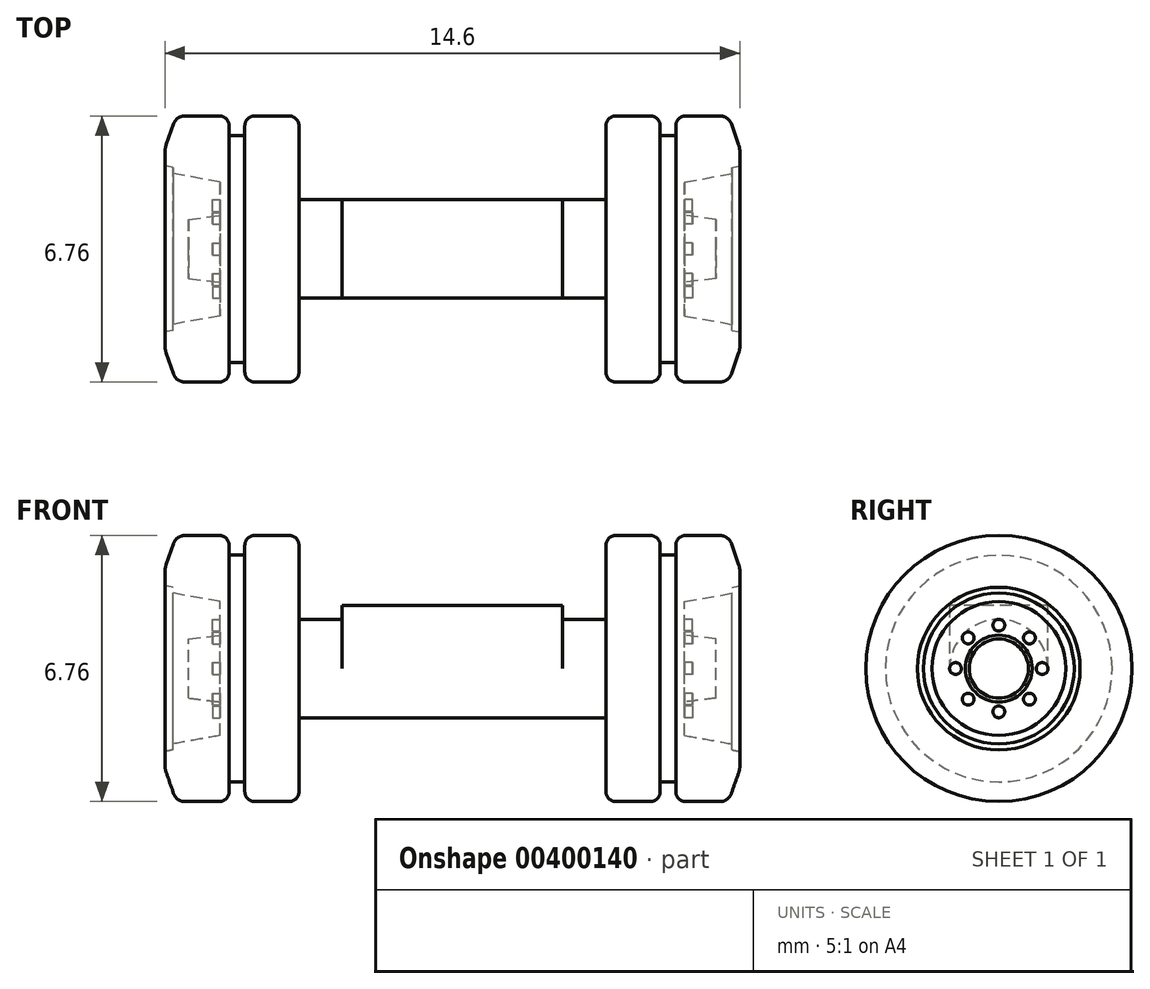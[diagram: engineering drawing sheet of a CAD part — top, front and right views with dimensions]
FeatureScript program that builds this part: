
annotation { "Feature Type Name" : "Feature", "Feature Type Description" : "" }
export const myFeature = defineFeature(function(context is Context, id is Id, definition is map)
    precondition{}
    {
        {
            var Q0;
            Q0=qCreatedBy(makeId("Front.planeOp"),FACE);
            var sketch = newSketch(context, id + "F0", { "sketchPlane" : qUnion([Q0])});
            skLineSegment(sketch, "E0", {"start": v(0, 0) * mm, "end": v(-36.36, 0) * mm, "construction": true});
            skLineSegment(sketch, "E1", {"start": v(0, 0) * mm, "end": v(0, 0.75) * mm});
            skLineSegment(sketch, "E2", {"start": v(-0.8, 0.85) * mm, "end": v(-0.8, 1.7) * mm});
            skLineSegment(sketch, "E3", {"start": v(-0.8, 1.7) * mm, "end": v(0.4, 1.92) * mm});
            skLineSegment(sketch, "E4", {"start": v(0.6, 2.15) * mm, "end": v(0.6, 2.48) * mm});
            skLineSegment(sketch, "E5", {"start": v(0.1, 3.38) * mm, "end": v(-0.78, 3.38) * mm});
            skLineSegment(sketch, "E6", {"start": v(-1.03, 3.13) * mm, "end": v(-1.03, 2.88) * mm});
            skLineSegment(sketch, "E7", {"start": v(-1.03, 2.88) * mm, "end": v(-1.43, 2.88) * mm});
            skLineSegment(sketch, "E8", {"start": v(-1.43, 2.88) * mm, "end": v(-1.43, 3.13) * mm});
            skLineSegment(sketch, "E9", {"start": v(-1.67, 3.38) * mm, "end": v(-2.55, 3.38) * mm});
            skLineSegment(sketch, "E10", {"start": v(-2.8, 3.13) * mm, "end": v(-2.8, 1.25) * mm});
            skLineSegment(sketch, "E11", {"start": v(-3.9, 1.25) * mm, "end": v(-3.9, 0) * mm});
            skLineSegment(sketch, "E12", {"start": v(-3.9, 0) * mm, "end": v(0, 0) * mm});
            skLineSegment(sketch, "E13", {"start": v(0.4, 1.92) * mm, "end": v(0.4, 2.07) * mm});
            skLineSegment(sketch, "E14", {"start": v(0.4, 2.07) * mm, "end": v(0.56, 2.1) * mm});
            skLineSegment(sketch, "E15", {"start": v(-3.9, 1.25) * mm, "end": v(-2.8, 1.25) * mm});
            skPoint(sketch, "E16.visualSharp", {"position": v(0.6, 3.38) * mm});
            skPoint(sketch, "E17.visualSharp", {"position": v(-2.8, 3.38) * mm});
            skArc(sketch, "E17.filletArc", {"start": v(-2.55, 3.38) * mm, "mid": v(-2.73, 3.3) * mm, "end": v(-2.8, 3.13) * mm});
            skPoint(sketch, "E18.visualSharp", {"position": v(-1.03, 3.38) * mm});
            skArc(sketch, "E18.filletArc", {"start": v(-0.78, 3.38) * mm, "mid": v(-0.95, 3.3) * mm, "end": v(-1.03, 3.13) * mm});
            skPoint(sketch, "E19.visualSharp", {"position": v(-1.43, 3.38) * mm});
            skArc(sketch, "E19.filletArc", {"start": v(-1.42, 3.13) * mm, "mid": v(-1.5, 3.3) * mm, "end": v(-1.67, 3.38) * mm});
            skPoint(sketch, "E20.visualSharp", {"position": v(0.6, 2.1) * mm});
            skArc(sketch, "E20.filletArc", {"start": v(0.56, 2.1) * mm, "mid": v(0.59, 2.12) * mm, "end": v(0.6, 2.15) * mm});
            skLineSegment(sketch, "E21", {"start": v(0.38, 3.18) * mm, "end": v(0.57, 2.65) * mm});
            skPoint(sketch, "E22.visualSharp", {"position": v(0.6, 2.57) * mm});
            skArc(sketch, "E22.filletArc", {"start": v(0.6, 2.48) * mm, "mid": v(0.6, 2.56) * mm, "end": v(0.57, 2.65) * mm});
            skPoint(sketch, "E23.visualSharp", {"position": v(0.31, 3.38) * mm});
            skArc(sketch, "E23.filletArc", {"start": v(0.38, 3.18) * mm, "mid": v(0.27, 3.32) * mm, "end": v(0.1, 3.38) * mm});
            skLineSegment(sketch, "E24", {"start": v(-0.8, 0.85) * mm, "end": v(0, 0.75) * mm});
            skSolve(sketch);
        }
        {
            var Q0;
            Q0=qSketchRegion(id+"F0",true);
            var Q1;
            Q1=sQuery(id+"F0.wireOp",EDGE,"E0");
            revolve(context, id + "F1", {"entities" : qUnion([Q0]), "axis" : qUnion([Q1]), "revolveType" : RevolveType.FULL});
        }
        {
            var Q0;
            Q0=makeQuery(id+"F1.opRevolve","SWEPT_FACE",FACE,{"disambiguationData":[OSD([sQuery(id+"F0.wireOp",EDGE,"E2")])]});
            var sketch = newSketch(context, id + "F2", { "sketchPlane" : qUnion([Q0])});
            skCircle(sketch, "E25", {"center": v(0, 0) * mm, "radius": 1.1 * mm, "construction": true});
            skCircle(sketch, "E26", {"center": v(0, 1.1) * mm, "radius": 0.15 * mm});
            skSolve(sketch);
        }
        {
            var Q0;
            Q0=qSketchRegion(id+"F2",true);
            extrude(context, id + "F3", {"entities" : qUnion([Q0]), "operationType" : NewBodyOperationType.ADD, "depth" : 0.2 * mm});
        }
        {
            var Q0;
            Q0=makeQuery(id+"F1.opRevolve","SWEPT_BODY",BODY,{"disambiguationData":[OSD([sQuery(id+"F0.wireOp",EDGE,"E1"),sQuery(id+"F0.wireOp",EDGE,"9i6tZyW2-yzXX-9EZJ-h79J-1cwnScpkviuc"),sQuery(id+"F0.wireOp",EDGE,"HbyUoBcI-ubs4-mTwl-hbnX-KPwjTuaUvTQE"),sQuery(id+"F0.wireOp",EDGE,"AccDx7tV-JdvI-fhYc-sTzn-GkBhagOZLKRE"),sQuery(id+"F0.wireOp",EDGE,"E2"),sQuery(id+"F0.wireOp",EDGE,"E3"),sQuery(id+"F0.wireOp",EDGE,"E4"),sQuery(id+"F0.wireOp",EDGE,"E5"),sQuery(id+"F0.wireOp",EDGE,"E6"),sQuery(id+"F0.wireOp",EDGE,"E7"),sQuery(id+"F0.wireOp",EDGE,"E8"),sQuery(id+"F0.wireOp",EDGE,"E9"),sQuery(id+"F0.wireOp",EDGE,"E10"),sQuery(id+"F0.wireOp",EDGE,"E11"),sQuery(id+"F0.wireOp",EDGE,"MRLpm4EO-d1Rz-y1Wd-tjo4-32WrfEVe7Kie"),sQuery(id+"F0.wireOp",EDGE,"1fY617z1-xQKE-QZae-sQAy-9TSEcJzTBgR6"),sQuery(id+"F0.wireOp",EDGE,"E12"),sQuery(id+"F0.wireOp",EDGE,"E13"),sQuery(id+"F0.wireOp",EDGE,"E14"),sQuery(id+"F0.wireOp",EDGE,"E15")])]});
            var Q1;
            Q1=makeQuery(id+"F1.opRevolve","SWEPT_FACE",FACE,{"disambiguationData":[OSD([sQuery(id+"F0.wireOp",EDGE,"E5")])]});
            circularPattern(context, id + "F4", {"operationType" : NewBodyOperationType.ADD, "entities" : qUnion([Q0]), "axis" : qUnion([Q1]), "angle" : 360 * degree, "instanceCount" : 8, "equalSpace" : true});
        }
        {
            var Q0;
            Q0=makeQuery(id+"F1.opRevolve","SWEPT_FACE",FACE,{"disambiguationData":[OSD([sQuery(id+"F0.wireOp",EDGE,"E11")])]});
            var sketch = newSketch(context, id + "F5", { "sketchPlane" : qUnion([Q0])});
            skArc(sketch, "E27.0", {"start": v(-1.25, 0) * mm, "mid": v(0, -1.25) * mm, "end": v(1.25, 0) * mm});
            skLineSegment(sketch, "E28", {"start": v(-1.25, 0) * mm, "end": v(-1.25, 1.6) * mm});
            skLineSegment(sketch, "E29", {"start": v(-1.25, 1.6) * mm, "end": v(1.25, 1.6) * mm});
            skLineSegment(sketch, "E30", {"start": v(1.25, 1.6) * mm, "end": v(1.25, 0) * mm});
            skSolve(sketch);
        }
        {
            var Q0;
            Q0=qSketchRegion(id+"F5",true);
            extrude(context, id + "F6", {"entities" : qUnion([Q0]), "operationType" : NewBodyOperationType.ADD, "depth" : 2.8 * mm});
        }
        {
            var Q0;
            Q0=makeQuery(id+"F1.opRevolve","SWEPT_BODY",BODY,{"disambiguationData":[OSD([sQuery(id+"F0.wireOp",EDGE,"E1"),sQuery(id+"F0.wireOp",EDGE,"9i6tZyW2-yzXX-9EZJ-h79J-1cwnScpkviuc"),sQuery(id+"F0.wireOp",EDGE,"HbyUoBcI-ubs4-mTwl-hbnX-KPwjTuaUvTQE"),sQuery(id+"F0.wireOp",EDGE,"AccDx7tV-JdvI-fhYc-sTzn-GkBhagOZLKRE"),sQuery(id+"F0.wireOp",EDGE,"E2"),sQuery(id+"F0.wireOp",EDGE,"E3"),sQuery(id+"F0.wireOp",EDGE,"E4"),sQuery(id+"F0.wireOp",EDGE,"E5"),sQuery(id+"F0.wireOp",EDGE,"E6"),sQuery(id+"F0.wireOp",EDGE,"E7"),sQuery(id+"F0.wireOp",EDGE,"E8"),sQuery(id+"F0.wireOp",EDGE,"E9"),sQuery(id+"F0.wireOp",EDGE,"E10"),sQuery(id+"F0.wireOp",EDGE,"E11"),sQuery(id+"F0.wireOp",EDGE,"E12"),sQuery(id+"F0.wireOp",EDGE,"E13"),sQuery(id+"F0.wireOp",EDGE,"E14"),sQuery(id+"F0.wireOp",EDGE,"E15"),sQuery(id+"F0.wireOp",EDGE,"E16.filletArc"),sQuery(id+"F0.wireOp",EDGE,"E17.filletArc"),sQuery(id+"F0.wireOp",EDGE,"E18.filletArc"),sQuery(id+"F0.wireOp",EDGE,"E19.filletArc"),sQuery(id+"F0.wireOp",EDGE,"E20.filletArc")])]});
            var Q1;
            Q1=makeQuery(id+"F6.opExtrude","CAP_FACE",FACE,{"disambiguationData":[OSD([sQuery(id+"F5.wireOp",EDGE,"E27.0"),sQuery(id+"F5.wireOp",EDGE,"E28"),sQuery(id+"F5.wireOp",EDGE,"E29"),sQuery(id+"F5.wireOp",EDGE,"E30")])],"isStart":false});
            mirror(context, id + "F7", {"operationType" : NewBodyOperationType.ADD, "entities" : qUnion([Q0]), "mirrorPlane" : qUnion([Q1])});
        }
    });
